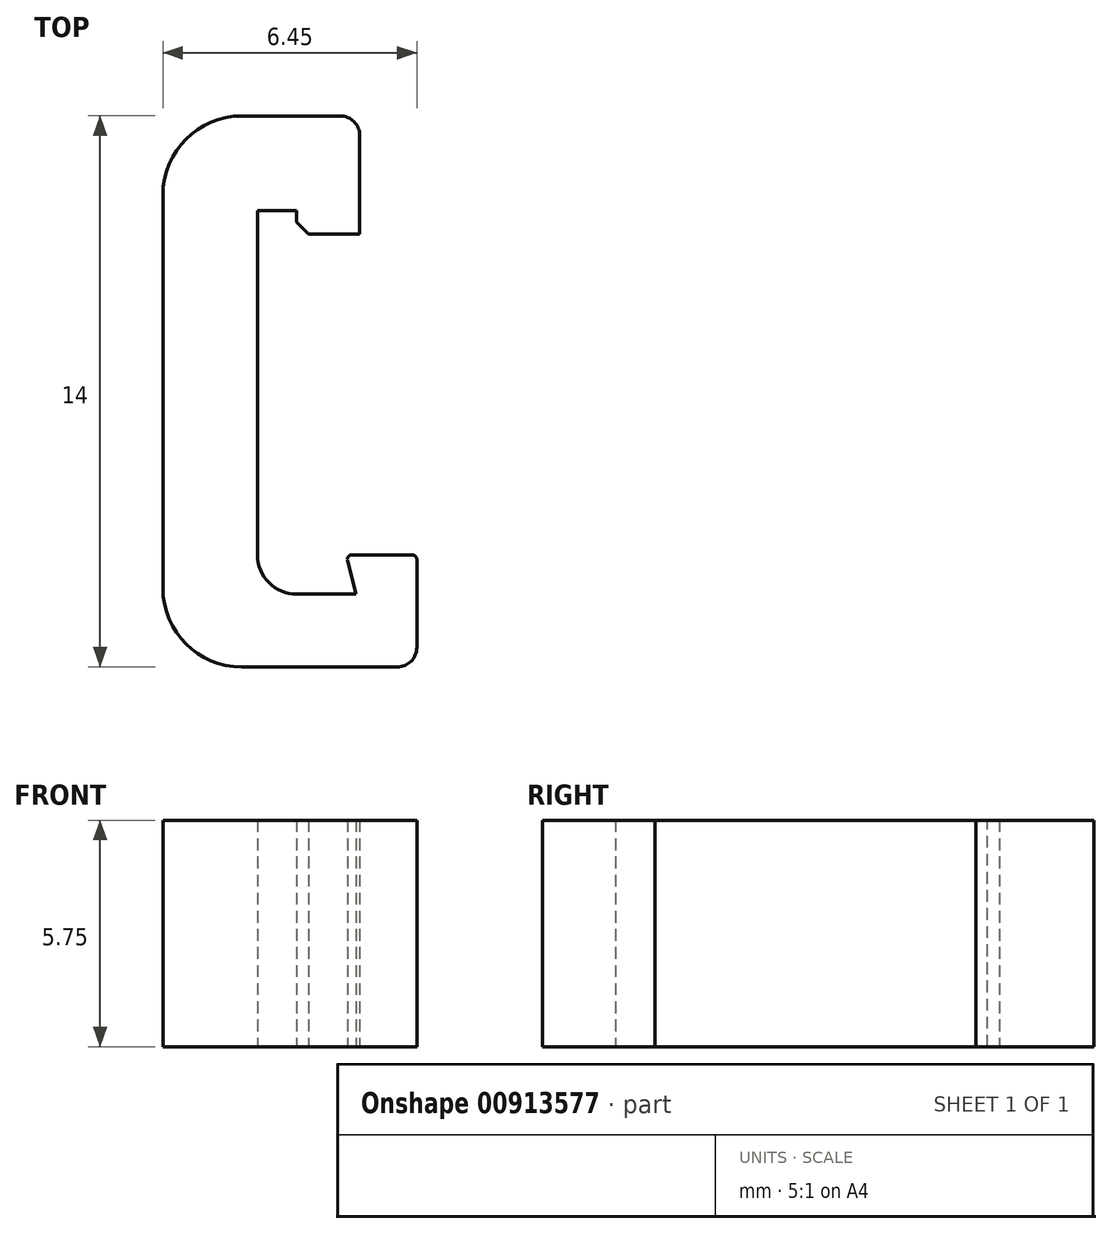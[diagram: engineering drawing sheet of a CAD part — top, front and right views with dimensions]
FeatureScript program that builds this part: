
annotation { "Feature Type Name" : "Feature", "Feature Type Description" : "" }
export const myFeature = defineFeature(function(context is Context, id is Id, definition is map)
    precondition{}
    {
        {
            var Q0;
            Q0=qCreatedBy(makeId("Top.planeOp"),FACE);
            var sketch = newSketch(context, id + "F0", { "sketchPlane" : qUnion([Q0])});
            skLineSegment(sketch, "E0", {"start": v(-0.48, 4.08) * mm, "end": v(1.12, 4.08) * mm});
            skLineSegment(sketch, "E1", {"start": v(1.12, 4.08) * mm, "end": v(1.12, 7.08) * mm});
            skLineSegment(sketch, "E2", {"start": v(1.12, 7.08) * mm, "end": v(-1.88, 7.08) * mm});
            skLineSegment(sketch, "E3", {"start": v(-3.88, 5.08) * mm, "end": v(-3.88, -4.92) * mm});
            skLineSegment(sketch, "E4", {"start": v(-1.88, -6.92) * mm, "end": v(2.57, -6.92) * mm});
            skLineSegment(sketch, "E5", {"start": v(2.57, -6.92) * mm, "end": v(2.57, -4.07) * mm});
            skLineSegment(sketch, "E6", {"start": v(2.57, -4.07) * mm, "end": v(0.77, -4.07) * mm});
            skLineSegment(sketch, "E7", {"start": v(0.77, -4.07) * mm, "end": v(1.02, -5.07) * mm});
            skLineSegment(sketch, "E8", {"start": v(1.02, -5.07) * mm, "end": v(-0.48, -5.07) * mm});
            skLineSegment(sketch, "E9", {"start": v(-1.48, -4.07) * mm, "end": v(-1.48, 4.68) * mm});
            skLineSegment(sketch, "E10", {"start": v(-1.48, 4.68) * mm, "end": v(-0.48, 4.68) * mm});
            skLineSegment(sketch, "E11", {"start": v(-0.48, 4.68) * mm, "end": v(-0.48, 4.08) * mm});
            skPoint(sketch, "E12.visualSharp", {"position": v(-1.48, -5.07) * mm});
            skArc(sketch, "E12.filletArc", {"start": v(-1.48, -4.07) * mm, "mid": v(-1.19, -4.78) * mm, "end": v(-0.48, -5.07) * mm});
            skPoint(sketch, "E13.visualSharp", {"position": v(-3.88, -6.92) * mm});
            skArc(sketch, "E13.filletArc", {"start": v(-3.88, -4.92) * mm, "mid": v(-3.3, -6.34) * mm, "end": v(-1.88, -6.92) * mm});
            skPoint(sketch, "E14.visualSharp", {"position": v(-3.88, 7.08) * mm});
            skArc(sketch, "E14.filletArc", {"start": v(-1.88, 7.08) * mm, "mid": v(-3.3, 6.5) * mm, "end": v(-3.88, 5.08) * mm});
            skSolve(sketch);
        }
        {
            var Q0;
            Q0 = qSketchRegion(id + "F0", true);
            extrude(context, id + "F1", {"entities" : qUnion([Q0]), "depth" : 5.75 * mm, "offsetDistance" : 25 * mm});
        }
        {
            var Q0;
            Q0=makeQuery(id+"F1.opExtrude","SWEPT_EDGE",EDGE,{"disambiguationData":[OSD([sQuery(id+"F0.wireOp",EDGE,"E4"),sQuery(id+"F0.wireOp",EDGE,"E5")])]});
            var Q1;
            Q1=makeQuery(id+"F1.opExtrude","SWEPT_EDGE",EDGE,{"disambiguationData":[OSD([sQuery(id+"F0.wireOp",EDGE,"E1"),sQuery(id+"F0.wireOp",EDGE,"E2")])]});
            fillet(context, id + "F2", {"entities" : qUnion([Q0, Q1]), "radius" : .5 * mm, "tangentPropagation" : true, "allowEdgeOverflow" : false});
        }
        {
            var Q0;
            Q0=makeQuery(id+"F1.opExtrude","SWEPT_EDGE",EDGE,{"disambiguationData":[OSD([sQuery(id+"F0.wireOp",EDGE,"E0"),sQuery(id+"F0.wireOp",EDGE,"E11")])]});
            chamfer(context, id + "F3", {"entities" : qUnion([Q0]), "width" : .3 * mm, "tangentPropagation" : true});
        }
        {
            var Q0;
            Q0=makeQuery(id+"F1.opExtrude","SWEPT_EDGE",EDGE,{"disambiguationData":[OSD([sQuery(id+"F0.wireOp",EDGE,"E6"),sQuery(id+"F0.wireOp",EDGE,"E7")])]});
            var Q1;
            Q1=makeQuery(id+"F1.opExtrude","SWEPT_EDGE",EDGE,{"disambiguationData":[OSD([sQuery(id+"F0.wireOp",EDGE,"E5"),sQuery(id+"F0.wireOp",EDGE,"E6")])]});
            fillet(context, id + "F4", {"entities" : qUnion([Q0, Q1]), "radius" : .12 * mm, "tangentPropagation" : true, "allowEdgeOverflow" : false});
        }
    });
